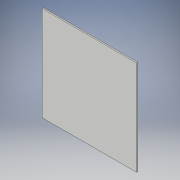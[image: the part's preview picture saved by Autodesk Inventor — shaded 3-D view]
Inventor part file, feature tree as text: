
AUTODESK INVENTOR PART (.ipt)
format: ipt  version: 2017 (Build 210142000, 142)  size: 88,576 bytes
history: native  units: in
note: dims shown in document units (in); Inventor stores cm internally (conversion verified against a paired STEP export)
features: extrude x1, sketch x1
ambient origin geometry x8: Origin, YZ Plane, XZ Plane, XY Plane, X Axis, Y Axis, Z Axis, Center Point
bodies: Solid1 (feature_tree)
feature tree (2):
  extrude  "Extrusion1"  Depth=36.0in
  sketch  "Sketch1"  dims[d0=36.0in d1=36.0in d2=0.5in d3=0.0in]
